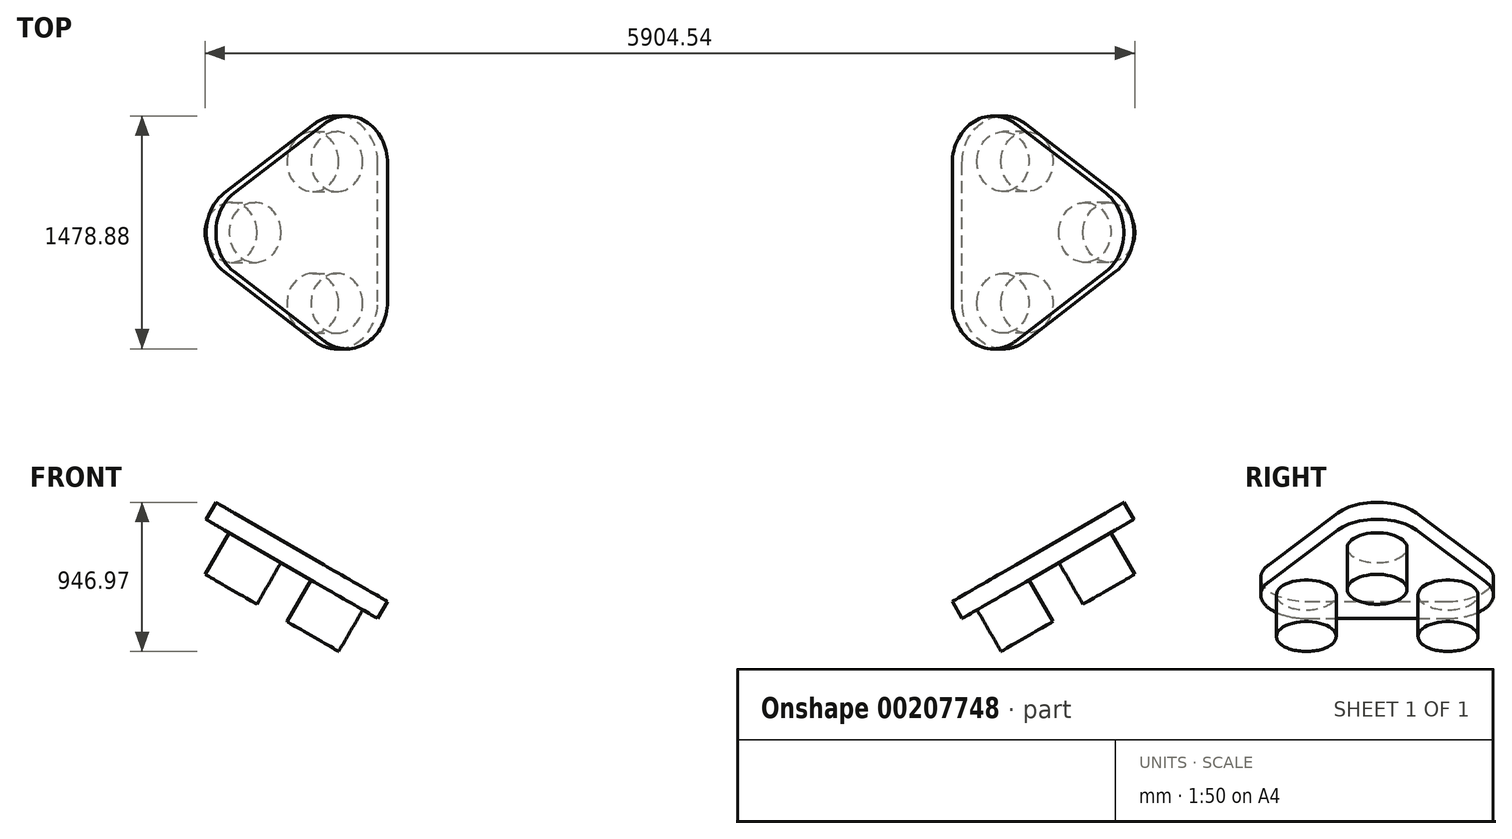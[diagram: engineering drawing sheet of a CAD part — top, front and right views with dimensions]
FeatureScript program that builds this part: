
annotation { "Feature Type Name" : "Feature", "Feature Type Description" : "" }
export const myFeature = defineFeature(function(context is Context, id is Id, definition is map)
    precondition{}
    {
        {
            var Q0;
            Q0=qCreatedBy(makeId("Top.planeOp"),FACE);
            cPlane(context, id + "F0", {"entities" : qUnion([Q0]), "cplaneType" : CPlaneType.OFFSET, "offset" : 305 * mm, "width" : 150 * mm, "height" : 150 * mm});
        }
        {
            var Q0;
            Q0=qCreatedBy(id+"F0.planeOp",FACE);
            var sketch = newSketch(context, id + "F1", { "sketchPlane" : qUnion([Q0])});
            skLineSegment(sketch, "E0.bottom", {"start": v(-1750, 1600) * mm, "end": v(1750, 1600) * mm, "construction": true});
            skLineSegment(sketch, "E0.top", {"start": v(-1750, -1600) * mm, "end": v(1750, -1600) * mm, "construction": true});
            skLineSegment(sketch, "E0.left", {"start": v(-1750, 1600) * mm, "end": v(-1750, -1600) * mm, "construction": true});
            skLineSegment(sketch, "E0.right", {"start": v(1750, 1600) * mm, "end": v(1750, -1600) * mm, "construction": true});
            skSolve(sketch);
        }
        {
            var Q0;
            Q0=sQuery(id+"F1.wireOp",EDGE,"E0.right");
            var Q1;
            Q1=qCreatedBy(id+"F0.planeOp",FACE);
            cPlane(context, id + "F2", {"entities" : qUnion([Q0, Q1]), "cplaneType" : CPlaneType.LINE_ANGLE, "offset" : 25 * mm, "angle" : 30 * degree, "width" : 150 * mm, "height" : 150 * mm});
        }
        {
            var Q0;
            Q0=qCreatedBy(id+"F2.planeOp",FACE);
            var sketch = newSketch(context, id + "F3", { "sketchPlane" : qUnion([Q0])});
            skLineSegment(sketch, "E1", {"start": v(3218.04, 0) * mm, "end": v(1718.04, 1000) * mm});
            skLineSegment(sketch, "E2", {"start": v(1718.04, 1000) * mm, "end": v(1718.04, -1000) * mm});
            skLineSegment(sketch, "E3", {"start": v(1718.04, -1000) * mm, "end": v(3218.04, 0) * mm});
            skLineSegment(sketch, "E4", {"start": v(591.92, 0) * mm, "end": v(3218.04, 0) * mm, "construction": true});
            skSolve(sketch);
        }
        {
            var Q0;
            Q0=makeQuery(id+"F3.imprint","IMPRINT",FACE,{"disambiguationData":[TD([[makeQuery(id+"F3.imprint","IMPRINT",EDGE,{"derivedFrom":sQuery(id+"F3.wireOp",EDGE,"E1")}),1.0]])]});
            extrude(context, id + "F4", {"entities" : qUnion([Q0]), "depth" : 125 * mm, "offsetDistance" : 25 * mm});
        }
        {
            var Q0;
            Q0=makeQuery(id+"F4.opExtrude","SWEPT_EDGE",EDGE,{"disambiguationData":[OSD([sQuery(id+"F3.wireOp",EDGE,"E1"),sQuery(id+"F3.wireOp",EDGE,"E3")])]});
            var Q1;
            Q1=makeQuery(id+"F4.opExtrude","SWEPT_EDGE",EDGE,{"disambiguationData":[OSD([sQuery(id+"F3.wireOp",EDGE,"E1"),sQuery(id+"F3.wireOp",EDGE,"E2")])]});
            var Q2;
            Q2=makeQuery(id+"F4.opExtrude","SWEPT_EDGE",EDGE,{"disambiguationData":[OSD([sQuery(id+"F3.wireOp",EDGE,"E2"),sQuery(id+"F3.wireOp",EDGE,"E3")])]});
            fillet(context, id + "F5", {"entities" : qUnion([Q0, Q1, Q2]), "radius" : 300 * mm, "tangentPropagation" : true, "allowEdgeOverflow" : false});
        }
        {
            var Q0;
            Q0=makeQuery(id+"F4.opExtrude","CAP_FACE",FACE,{"disambiguationData":[OSD([sQuery(id+"F3.wireOp",EDGE,"E1"),sQuery(id+"F3.wireOp",EDGE,"E2"),sQuery(id+"F3.wireOp",EDGE,"E3")])],"isStart":false});
            var sketch = newSketch(context, id + "F6", { "sketchPlane" : qUnion([Q0])});
            skCircle(sketch, "E5", {"center": v(2618.04, 0) * mm, "radius": 190 * mm});
            skCircle(sketch, "E6", {"center": v(2018.04, -450) * mm, "radius": 190 * mm});
            skCircle(sketch, "E7", {"center": v(2018.04, 450) * mm, "radius": 190 * mm});
            skSolve(sketch);
        }
        {
            var Q0;
            Q0 = qSketchRegion(id + "F6", true);
            extrude(context, id + "F7", {"entities" : qUnion([Q0]), "operationType" : NewBodyOperationType.ADD, "depth" : 305 * mm, "offsetDistance" : 25 * mm});
        }
        {
            var Q0;
            Q0=makeQuery(id+"F4.opExtrude","SWEPT_BODY",BODY,{"disambiguationData":[OSD([sQuery(id+"F3.wireOp",EDGE,"E1"),sQuery(id+"F3.wireOp",EDGE,"E2"),sQuery(id+"F3.wireOp",EDGE,"E3")])]});
            var Q1;
            Q1=qCreatedBy(makeId("Right.planeOp"),FACE);
            mirror(context, id + "F8", {"entities" : qUnion([Q0]), "mirrorPlane" : qUnion([Q1])});
        }
    });
